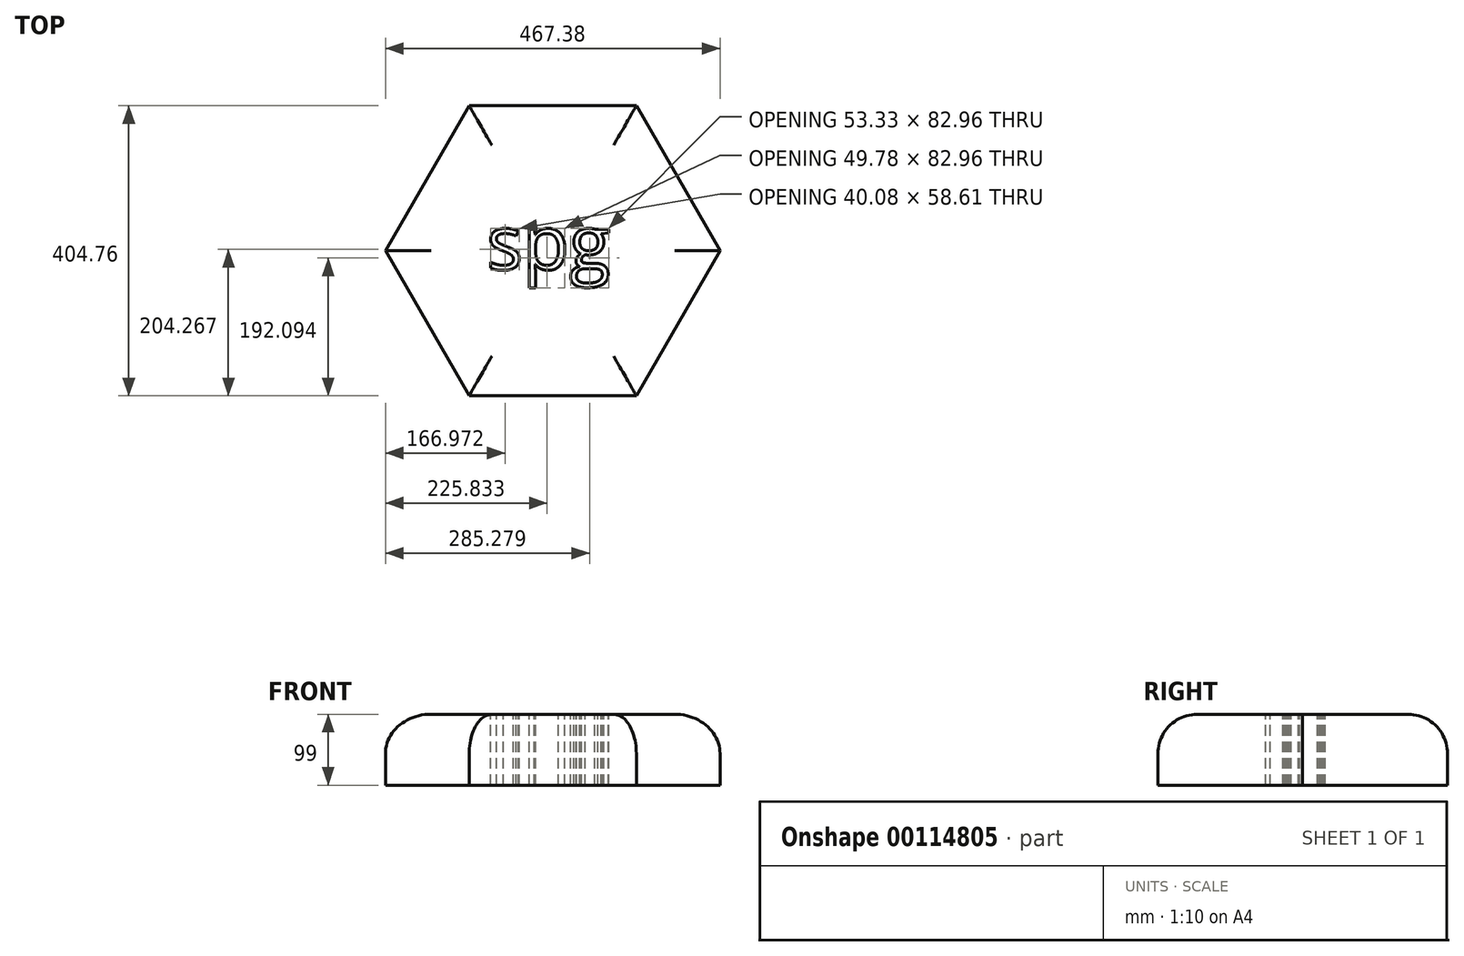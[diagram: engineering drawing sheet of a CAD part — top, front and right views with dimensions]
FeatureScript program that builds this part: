
annotation { "Feature Type Name" : "Feature", "Feature Type Description" : "" }
export const myFeature = defineFeature(function(context is Context, id is Id, definition is map)
    precondition{}
    {
        {
            var Q0;
            Q0=qCreatedBy(makeId("Top.planeOp"),FACE);
            var sketch = newSketch(context, id + "F0", { "sketchPlane" : qUnion([Q0])});
            skCircle(sketch, "E0.cCircle", {"center": v(0, 202.38) * mm, "radius": 202.38 * mm, "construction": true});
            skLineSegment(sketch, "E0.0", {"start": v(116.85, 0) * mm, "end": v(-116.85, 0) * mm});
            skLineSegment(sketch, "E0.1", {"start": v(-116.85, 0) * mm, "end": v(-233.7, 202.38) * mm});
            skLineSegment(sketch, "E0.2", {"start": v(-233.7, 202.38) * mm, "end": v(-116.85, 404.76) * mm});
            skLineSegment(sketch, "E0.3", {"start": v(-116.85, 404.76) * mm, "end": v(116.85, 404.76) * mm});
            skLineSegment(sketch, "E0.4", {"start": v(116.85, 404.76) * mm, "end": v(233.7, 202.38) * mm});
            skLineSegment(sketch, "E0.5", {"start": v(233.7, 202.38) * mm, "end": v(116.85, 0) * mm});
            skPoint(sketch, "E0.0.midPoint", {"position": v(0, 0) * mm});
            skSolve(sketch);
        }
        {
            var Q0;
            Q0=makeQuery(id+"F0.imprint","IMPRINT",FACE,{"disambiguationData":[TD([[makeQuery(id+"F0.imprint","IMPRINT",EDGE,{"derivedFrom":sQuery(id+"F0.wireOp",EDGE,"E0.0")}),-1.0]])]});
            extrude(context, id + "F1", {"entities" : qUnion([Q0]), "depth" : 99 * mm});
        }
        {
            var Q0;
            Q0=makeQuery(id+"F1.opExtrude","CAP_FACE",FACE,{"disambiguationData":[OSD([sQuery(id+"F0.wireOp",EDGE,"E0.0"),sQuery(id+"F0.wireOp",EDGE,"E0.1"),sQuery(id+"F0.wireOp",EDGE,"E0.2"),sQuery(id+"F0.wireOp",EDGE,"E0.3"),sQuery(id+"F0.wireOp",EDGE,"E0.4"),sQuery(id+"F0.wireOp",EDGE,"E0.5")])],"isStart":false});
            fillet(context, id + "F2", {"entities" : qUnion([Q0]), "radius" : 55 * mm, "tangentPropagation" : true, "allowEdgeOverflow" : false});
        }
        {
            var Q0;
            Q0=makeQuery(id+"F1.opExtrude","CAP_FACE",FACE,{"disambiguationData":[OSD([sQuery(id+"F0.wireOp",EDGE,"E0.0"),sQuery(id+"F0.wireOp",EDGE,"E0.1"),sQuery(id+"F0.wireOp",EDGE,"E0.2"),sQuery(id+"F0.wireOp",EDGE,"E0.3"),sQuery(id+"F0.wireOp",EDGE,"E0.4"),sQuery(id+"F0.wireOp",EDGE,"E0.5")])],"isStart":false});
            var sketch = newSketch(context, id + "F3", { "sketchPlane" : qUnion([Q0])});
            skText(sketch, "E1", { "text": "spg", "fontName": "OpenSans-Regular.ttf"});
            const initialGuessF3  = {"E1": [-0.09222, 0.176, 1, 0, 0.07606]};
            skSetInitialGuess(sketch, initialGuessF3);
            skSolve(sketch);
        }
        {
            var Q0;
            Q0 = qSketchRegion(id + "F3", true);
            extrude(context, id + "F4", {"entities" : qUnion([Q0]), "operationType" : NewBodyOperationType.REMOVE, "endBound" : BoundingType.THROUGH_ALL, "oppositeDirection" : true, "depth" : 25 * mm});
        }
    });
